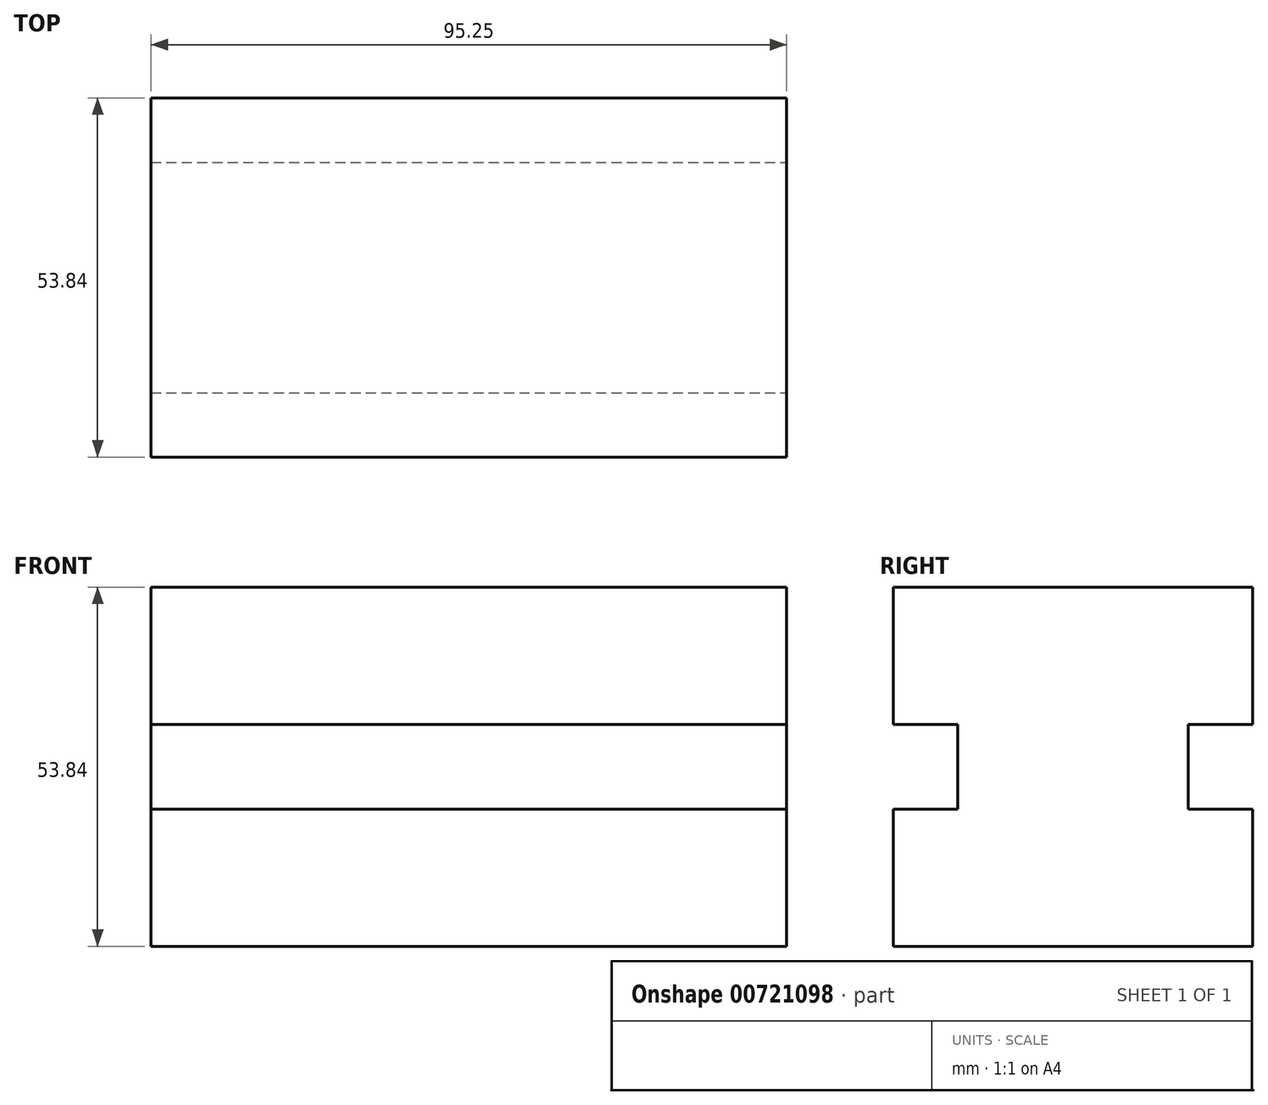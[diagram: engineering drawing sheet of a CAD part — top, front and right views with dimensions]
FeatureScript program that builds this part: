
annotation { "Feature Type Name" : "Feature", "Feature Type Description" : "" }
export const myFeature = defineFeature(function(context is Context, id is Id, definition is map)
    precondition{}
    {
        {
            var Q0;
            Q0=qCreatedBy(makeId("Right.planeOp"),FACE);
            var sketch = newSketch(context, id + "F0", { "sketchPlane" : qUnion([Q0])});
            skLineSegment(sketch, "E0.bottom", {"start": v(26.92, -26.92) * mm, "end": v(-26.92, -26.92) * mm});
            skLineSegment(sketch, "E0.top", {"start": v(26.92, 26.92) * mm, "end": v(-26.92, 26.92) * mm});
            skLineSegment(sketch, "E0.left", {"start": v(26.92, -26.92) * mm, "end": v(26.92, -6.35) * mm});
            skLineSegment(sketch, "E0.right", {"start": v(-26.92, -26.92) * mm, "end": v(-26.92, -6.35) * mm});
            skPoint(sketch, "E0.middle", {"position": v(0, 0) * mm});
            skLineSegment(sketch, "E1.bottom", {"start": v(-26.92, 6.35) * mm, "end": v(-17.27, 6.35) * mm});
            skLineSegment(sketch, "E1.top", {"start": v(-26.92, -6.35) * mm, "end": v(-17.27, -6.35) * mm});
            skLineSegment(sketch, "E1.right", {"start": v(-17.27, 6.35) * mm, "end": v(-17.27, -6.35) * mm});
            skLineSegment(sketch, "E2", {"start": v(0, 32.68) * mm, "end": v(0, -52.22) * mm, "construction": true});
            skPoint(sketch, "E2.startSnap0", {"position": v(0, 26.92) * mm});
            skLineSegment(sketch, "E3.MirrorCS", {"start": v(26.92, 6.35) * mm, "end": v(17.27, 6.35) * mm});
            skLineSegment(sketch, "E4.MirrorCS", {"start": v(17.27, 6.35) * mm, "end": v(17.27, -6.35) * mm});
            skLineSegment(sketch, "E5.MirrorCS", {"start": v(26.92, -6.35) * mm, "end": v(17.27, -6.35) * mm});
            skLineSegment(sketch, "E6.trimOffspring", {"start": v(-26.92, 6.35) * mm, "end": v(-26.92, 26.92) * mm});
            skLineSegment(sketch, "E7.trimOffspring", {"start": v(26.92, 6.35) * mm, "end": v(26.92, 26.92) * mm});
            skSolve(sketch);
        }
        {
            var Q0;
            Q0=makeQuery(id+"F0.imprint","IMPRINT",FACE,{"disambiguationData":[TD([[makeQuery(id+"F0.imprint","IMPRINT",EDGE,{"derivedFrom":sQuery(id+"F0.wireOp",EDGE,"E0.bottom")}),-1.0]])]});
            extrude(context, id + "F1", {"entities" : qUnion([Q0]), "oppositeDirection" : true, "depth" : 95.25 * mm, "offsetDistance" : 25.4 * mm});
        }
    });
